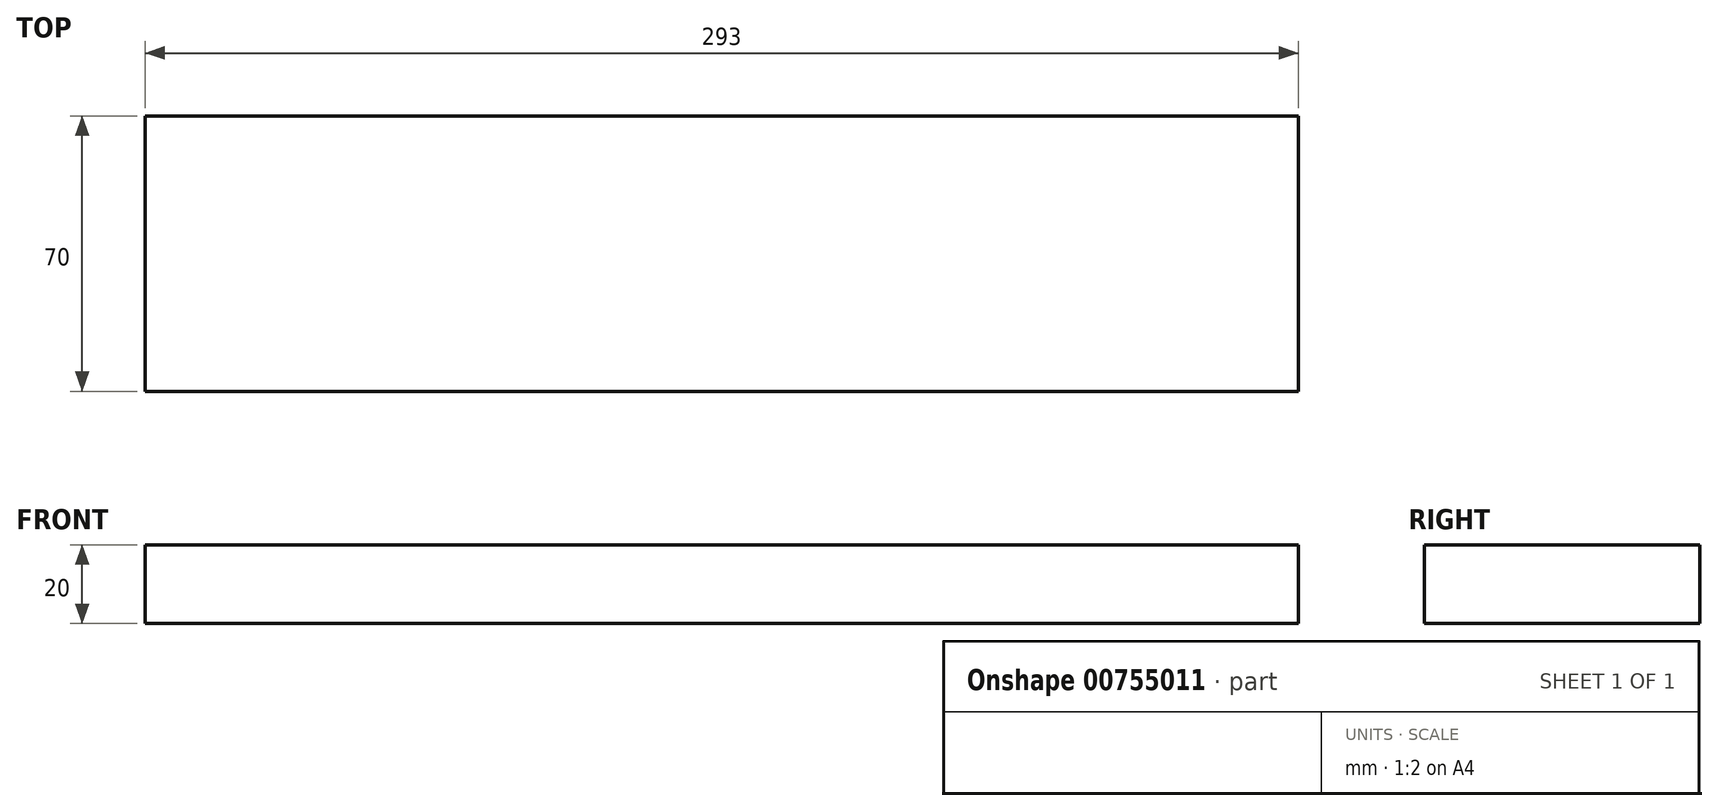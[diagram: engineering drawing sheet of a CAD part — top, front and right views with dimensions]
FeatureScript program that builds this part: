
annotation { "Feature Type Name" : "Feature", "Feature Type Description" : "" }
export const myFeature = defineFeature(function(context is Context, id is Id, definition is map)
    precondition{}
    {
        {
            var Q0;
            Q0=qCreatedBy(makeId("Top.planeOp"),FACE);
            var sketch = newSketch(context, id + "F0", { "sketchPlane" : qUnion([Q0])});
            skLineSegment(sketch, "E0.bottom", {"start": v(-231.73, 15.15) * mm, "end": v(61.27, 15.15) * mm});
            skLineSegment(sketch, "E0.top", {"start": v(-231.73, -54.85) * mm, "end": v(61.27, -54.85) * mm});
            skLineSegment(sketch, "E0.left", {"start": v(-231.73, 15.15) * mm, "end": v(-231.73, -54.85) * mm});
            skLineSegment(sketch, "E0.right", {"start": v(61.27, 15.15) * mm, "end": v(61.27, -54.85) * mm});
            skSolve(sketch);
        }
        {
            var Q0;
            Q0 = qSketchRegion(id + "F0", true);
            extrude(context, id + "F1", {"entities" : qUnion([Q0]), "depth" : 20 * mm, "offsetDistance" : 25 * mm});
        }
    });
